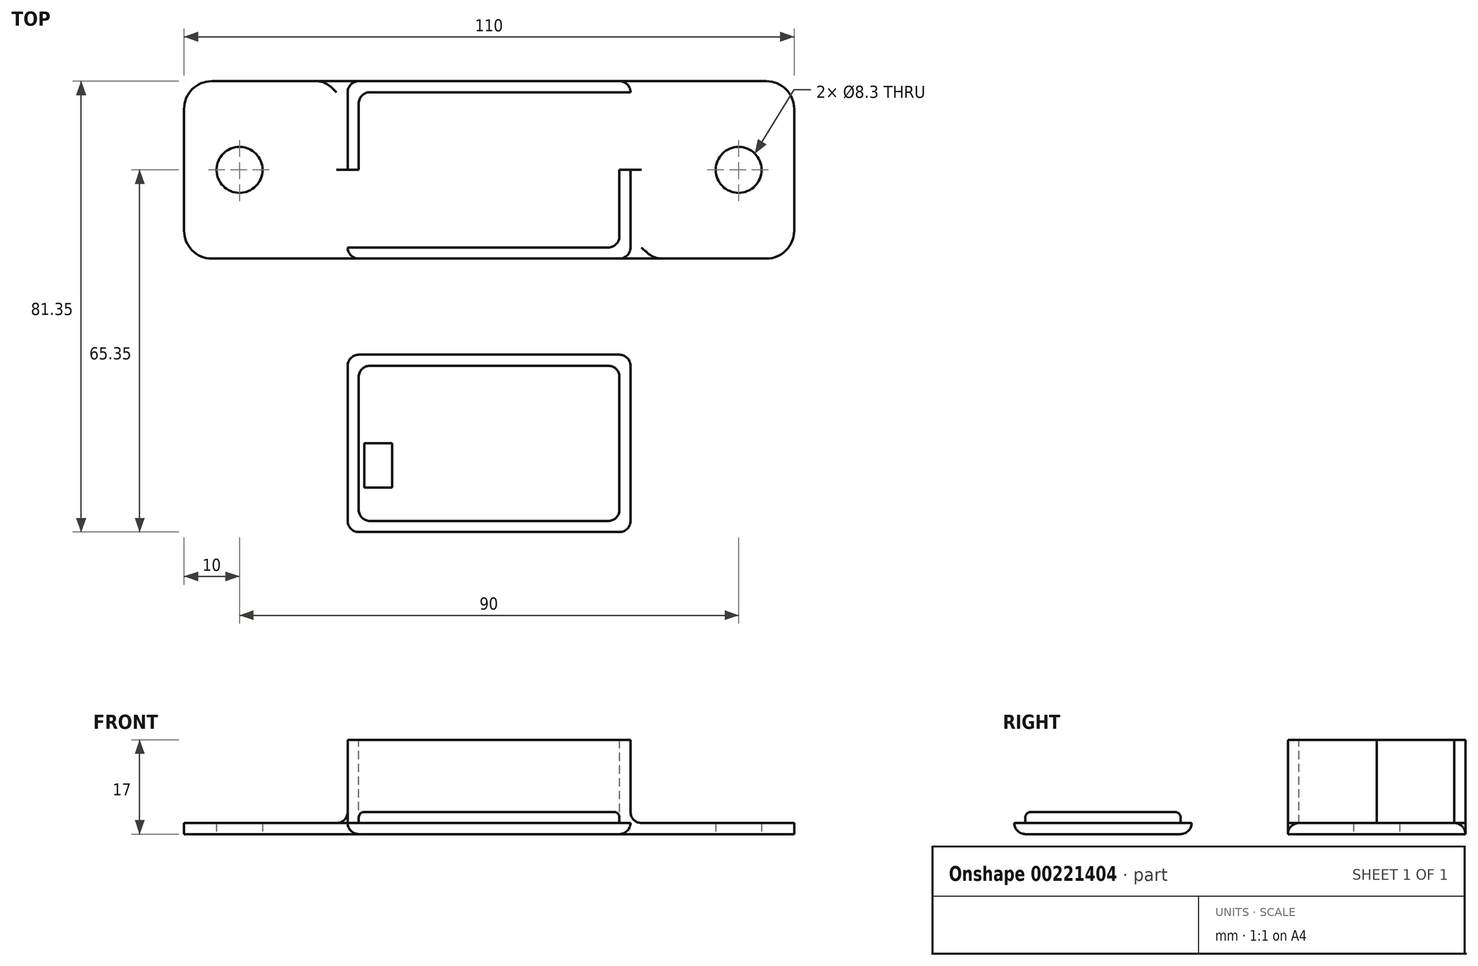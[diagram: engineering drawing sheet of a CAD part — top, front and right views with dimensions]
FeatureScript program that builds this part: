
annotation { "Feature Type Name" : "Feature", "Feature Type Description" : "" }
export const myFeature = defineFeature(function(context is Context, id is Id, definition is map)
    precondition{}
    {
        {
            var Q0;
            Q0=qCreatedBy(makeId("Top.planeOp"),FACE);
            var sketch = newSketch(context, id + "F0", { "sketchPlane" : qUnion([Q0])});
            skLineSegment(sketch, "E0.bottom", {"start": v(55, 16) * mm, "end": v(-55, 16) * mm});
            skLineSegment(sketch, "E0.top", {"start": v(55, -16) * mm, "end": v(-55, -16) * mm});
            skLineSegment(sketch, "E0.left", {"start": v(55, 16) * mm, "end": v(55, -16) * mm});
            skLineSegment(sketch, "E0.right", {"start": v(-55, 16) * mm, "end": v(-55, -16) * mm});
            skPoint(sketch, "E0.middle", {"position": v(0, 0) * mm});
            skLineSegment(sketch, "E1", {"start": v(0, 0) * mm, "end": v(45, 0) * mm});
            skLineSegment(sketch, "E2", {"start": v(0, 0) * mm, "end": v(-45, 0) * mm});
            skCircle(sketch, "E3", {"center": v(-45, 0) * mm, "radius": 4.15 * mm});
            skCircle(sketch, "E4", {"center": v(45, 0) * mm, "radius": 4.15 * mm});
            skSolve(sketch);
        }
        {
            var Q0;
            Q0 = qSketchRegion(id + "F0", true);
            extrude(context, id + "F1", {"entities" : qUnion([Q0]), "depth" : 2 * mm});
        }
        {
            var Q0;
            Q0=makeQuery(id+"F1.opExtrude","CAP_FACE",FACE,{"disambiguationData":[OSD([sQuery(id+"F0.wireOp",EDGE,"E0.bottom"),sQuery(id+"F0.wireOp",EDGE,"E0.top"),sQuery(id+"F0.wireOp",EDGE,"E0.left"),sQuery(id+"F0.wireOp",EDGE,"E0.right")])],"isStart":false});
            var sketch = newSketch(context, id + "F2", { "sketchPlane" : qUnion([Q0])});
            skLineSegment(sketch, "E5", {"start": v(0, -16) * mm, "end": v(0, 16) * mm});
            skLineSegment(sketch, "E6.bottom", {"start": v(23.5, 16) * mm, "end": v(-23.5, 16) * mm});
            skLineSegment(sketch, "E6.top", {"start": v(23.5, -16) * mm, "end": v(-23.5, -16) * mm});
            skLineSegment(sketch, "E6.left", {"start": v(23.5, 16) * mm, "end": v(23.5, -16) * mm});
            skLineSegment(sketch, "E6.right", {"start": v(-23.5, 16) * mm, "end": v(-23.5, -16) * mm});
            skPoint(sketch, "E6.middle", {"position": v(0, 0) * mm});
            skLineSegment(sketch, "E7.bottom", {"start": v(23.5, 14) * mm, "end": v(-23.5, 14) * mm});
            skLineSegment(sketch, "E7.top", {"start": v(23.5, -14) * mm, "end": v(-23.5, -14) * mm});
            skLineSegment(sketch, "E7.left", {"start": v(23.5, 14) * mm, "end": v(23.5, -14) * mm});
            skLineSegment(sketch, "E7.right", {"start": v(-23.5, 14) * mm, "end": v(-23.5, -14) * mm});
            skLineSegment(sketch, "E8.bottom", {"start": v(-25.5, 16) * mm, "end": v(25.5, 16) * mm});
            skLineSegment(sketch, "E8.top", {"start": v(-25.5, -16) * mm, "end": v(25.5, -16) * mm});
            skLineSegment(sketch, "E8.left", {"start": v(-25.5, 16) * mm, "end": v(-25.5, -16) * mm});
            skLineSegment(sketch, "E8.right", {"start": v(25.5, 16) * mm, "end": v(25.5, -16) * mm});
            skSolve(sketch);
        }
        {
            var Q0;
            Q0 = qSketchRegion(id + "F2", true);
            extrude(context, id + "F3", {"entities" : qUnion([Q0]), "operationType" : NewBodyOperationType.ADD, "depth" : 15 * mm});
        }
        {
            var Q0;
            Q0=makeQuery(id+"F3.opExtrude","SWEPT_FACE",FACE,{"disambiguationData":[OSD([sQuery(id+"F2.wireOp",EDGE,"E8.left")])]});
            var sketch = newSketch(context, id + "F4", { "sketchPlane" : qUnion([Q0])});
            skLineSegment(sketch, "E9.bottom", {"start": v(14, 2) * mm, "end": v(0, 2) * mm});
            skLineSegment(sketch, "E9.top", {"start": v(14, 17) * mm, "end": v(0, 17) * mm});
            skLineSegment(sketch, "E9.left", {"start": v(14, 2) * mm, "end": v(14, 17) * mm});
            skLineSegment(sketch, "E9.right", {"start": v(0, 2) * mm, "end": v(0, 17) * mm});
            skSolve(sketch);
        }
        {
            var Q0;
            Q0 = qSketchRegion(id + "F4", true);
            extrude(context, id + "F5", {"entities" : qUnion([Q0]), "operationType" : NewBodyOperationType.REMOVE, "endBound" : BoundingType.UP_TO_NEXT, "oppositeDirection" : true, "depth" : 25 * mm});
        }
        {
            var Q0;
            Q0=makeQuery(id+"F3.opExtrude","SWEPT_FACE",FACE,{"disambiguationData":[OSD([sQuery(id+"F2.wireOp",EDGE,"E8.right")])]});
            var sketch = newSketch(context, id + "F6", { "sketchPlane" : qUnion([Q0])});
            skLineSegment(sketch, "E10.bottom", {"start": v(14, 2) * mm, "end": v(0, 2) * mm});
            skLineSegment(sketch, "E10.top", {"start": v(14, 17) * mm, "end": v(0, 17) * mm});
            skLineSegment(sketch, "E10.left", {"start": v(14, 2) * mm, "end": v(14, 17) * mm});
            skLineSegment(sketch, "E10.right", {"start": v(0, 2) * mm, "end": v(0, 17) * mm});
            skSolve(sketch);
        }
        {
            var Q0;
            Q0 = qSketchRegion(id + "F6", true);
            extrude(context, id + "F7", {"entities" : qUnion([Q0]), "operationType" : NewBodyOperationType.REMOVE, "endBound" : BoundingType.UP_TO_NEXT, "oppositeDirection" : true, "depth" : 25 * mm});
        }
        {
            var Q0;
            Q0=makeQuery(id+"F1.opExtrude","SWEPT_EDGE",EDGE,{"disambiguationData":[OSD([sQuery(id+"F0.wireOp",EDGE,"E0.top"),sQuery(id+"F0.wireOp",EDGE,"E0.right")])]});
            var Q1;
            Q1=makeQuery(id+"F1.opExtrude","SWEPT_EDGE",EDGE,{"disambiguationData":[OSD([sQuery(id+"F0.wireOp",EDGE,"E0.bottom"),sQuery(id+"F0.wireOp",EDGE,"E0.right")])]});
            var Q2;
            Q2=makeQuery(id+"F1.opExtrude","SWEPT_EDGE",EDGE,{"disambiguationData":[OSD([sQuery(id+"F0.wireOp",EDGE,"E0.top"),sQuery(id+"F0.wireOp",EDGE,"E0.left")])]});
            var Q3;
            Q3=makeQuery(id+"F1.opExtrude","SWEPT_EDGE",EDGE,{"disambiguationData":[OSD([sQuery(id+"F0.wireOp",EDGE,"E0.bottom"),sQuery(id+"F0.wireOp",EDGE,"E0.left")])]});
            fillet(context, id + "F8", {"entities" : qUnion([Q0, Q1, Q2, Q3]), "radius" : 5 * mm, "tangentPropagation" : true, "allowEdgeOverflow" : false});
        }
        {
            var Q0;
            Q0=makeQuery(id+"F3.opExtrude","SWEPT_EDGE",EDGE,{"disambiguationData":[OSD([sQuery(id+"F0.wireOp",EDGE,"E0.top"),sQuery(id+"F2.wireOp",EDGE,"E8.top"),sQuery(id+"F2.wireOp",EDGE,"E8.right")])]});
            var Q1;
            Q1=makeQuery(id+"F3.opExtrude","SWEPT_EDGE",EDGE,{"disambiguationData":[OSD([sQuery(id+"F2.wireOp",EDGE,"E6.left"),sQuery(id+"F2.wireOp",EDGE,"E7.top"),sQuery(id+"F2.wireOp",EDGE,"E7.left")])]});
            var Q2;
            Q2=makeQuery(id+"F3.opExtrude","SWEPT_EDGE",EDGE,{"disambiguationData":[OSD([sQuery(id+"F2.wireOp",EDGE,"E6.right"),sQuery(id+"F2.wireOp",EDGE,"E7.bottom"),sQuery(id+"F2.wireOp",EDGE,"E7.right")])]});
            var Q3;
            Q3=makeQuery(id+"F3.opExtrude","SWEPT_EDGE",EDGE,{"disambiguationData":[OSD([sQuery(id+"F0.wireOp",EDGE,"E0.bottom"),sQuery(id+"F2.wireOp",EDGE,"E8.bottom"),sQuery(id+"F2.wireOp",EDGE,"E8.left")])]});
            var Q4;
            {var subQ0=sQuery(id+"F0.wireOp",EDGE,"E0.bottom");var subQ1=sQuery(id+"F2.wireOp",EDGE,"E8.left");Q4=makeQuery(id+"F5.boolean.opBoolean","SPLIT",EDGE,{"disambiguationData":[TD([makeQuery(id+"F1.opExtrude","SWEPT_FACE",FACE,{"disambiguationData":[OSD([subQ0])]})])],"derivedFrom":makeQuery(id+"F3.opExtrude","CAP_EDGE",EDGE,{"disambiguationData":[OSD([subQ1])],"isStart":true})});}
            var Q5;
            {var subQ0=sQuery(id+"F2.wireOp",EDGE,"E8.right");var subQ1=sQuery(id+"F0.wireOp",EDGE,"E0.top");Q5=makeQuery(id+"F7.boolean.opBoolean","SPLIT",EDGE,{"disambiguationData":[TD([makeQuery(id+"F1.opExtrude","SWEPT_FACE",FACE,{"disambiguationData":[OSD([subQ1])]})])],"derivedFrom":makeQuery(id+"F3.opExtrude","CAP_EDGE",EDGE,{"disambiguationData":[OSD([subQ0])],"isStart":true})});}
            var Q6;
            Q6=makeQuery(id+"F3.opExtrude","SWEPT_EDGE",EDGE,{"disambiguationData":[OSD([sQuery(id+"F0.wireOp",EDGE,"E0.bottom"),sQuery(id+"F2.wireOp",EDGE,"E8.bottom"),sQuery(id+"F2.wireOp",EDGE,"E8.right")])]});
            var Q7;
            Q7=makeQuery(id+"F3.opExtrude","SWEPT_EDGE",EDGE,{"disambiguationData":[OSD([sQuery(id+"F0.wireOp",EDGE,"E0.top"),sQuery(id+"F2.wireOp",EDGE,"E8.top"),sQuery(id+"F2.wireOp",EDGE,"E8.left")])]});
            fillet(context, id + "F9", {"entities" : qUnion([Q0, Q1, Q2, Q3, Q4, Q5, Q6, Q7]), "radius" : 2 * mm, "tangentPropagation" : true, "allowEdgeOverflow" : false});
        }
        {
            var Q0;
            Q0=qCreatedBy(makeId("Top.planeOp"),FACE);
            var sketch = newSketch(context, id + "F10", { "sketchPlane" : qUnion([Q0])});
            skLineSegment(sketch, "E11.bottom", {"start": v(23.5, -35.35) * mm, "end": v(-23.5, -35.35) * mm});
            skLineSegment(sketch, "E11.top", {"start": v(23.5, -63.35) * mm, "end": v(-23.5, -63.35) * mm});
            skLineSegment(sketch, "E11.left", {"start": v(23.5, -35.35) * mm, "end": v(23.5, -63.35) * mm});
            skLineSegment(sketch, "E11.right", {"start": v(-23.5, -35.35) * mm, "end": v(-23.5, -63.35) * mm});
            skPoint(sketch, "E11.middle", {"position": v(0, -49.35) * mm});
            skLineSegment(sketch, "E12.bottom", {"start": v(25.5, -33.35) * mm, "end": v(-25.5, -33.35) * mm});
            skLineSegment(sketch, "E12.top", {"start": v(25.5, -65.35) * mm, "end": v(-25.5, -65.35) * mm});
            skLineSegment(sketch, "E12.left", {"start": v(25.5, -33.35) * mm, "end": v(25.5, -65.35) * mm});
            skLineSegment(sketch, "E12.right", {"start": v(-25.5, -33.35) * mm, "end": v(-25.5, -65.35) * mm});
            skSolve(sketch);
        }
        {
            var Q0;
            Q0 = qSketchRegion(id + "F10", true);
            var Q1;
            Q1=makeQuery(id+"F10.imprint","IMPRINT",FACE,{"disambiguationData":[TD([[makeQuery(id+"F10.imprint","IMPRINT",EDGE,{"derivedFrom":sQuery(id+"F10.wireOp",EDGE,"E11.bottom")}),1.0]])]});
            extrude(context, id + "F11", {"entities" : qUnion([Q0, Q1]), "depth" : 2 * mm});
        }
        {
            var Q0;
            Q0=makeQuery(id+"F11.opExtrude","CAP_FACE",FACE,{"disambiguationData":[OSD([sQuery(id+"F10.wireOp",EDGE,"E12.bottom"),sQuery(id+"F10.wireOp",EDGE,"E12.top"),sQuery(id+"F10.wireOp",EDGE,"E12.left"),sQuery(id+"F10.wireOp",EDGE,"E12.right")])],"isStart":false});
            var sketch = newSketch(context, id + "F12", { "sketchPlane" : qUnion([Q0])});
            skLineSegment(sketch, "E13", {"start": v(0, -33.35) * mm, "end": v(0, -65.35) * mm});
            skLineSegment(sketch, "E14.bottom", {"start": v(23.5, -35.35) * mm, "end": v(-23.5, -35.35) * mm});
            skLineSegment(sketch, "E14.top", {"start": v(23.5, -63.35) * mm, "end": v(-23.5, -63.35) * mm});
            skLineSegment(sketch, "E14.left", {"start": v(23.5, -35.35) * mm, "end": v(23.5, -63.35) * mm});
            skLineSegment(sketch, "E14.right", {"start": v(-23.5, -35.35) * mm, "end": v(-23.5, -63.35) * mm});
            skPoint(sketch, "E14.middle", {"position": v(0, -49.35) * mm});
            skSolve(sketch);
        }
        {
            var Q0;
            Q0 = qSketchRegion(id + "F12", true);
            extrude(context, id + "F13", {"entities" : qUnion([Q0]), "operationType" : NewBodyOperationType.ADD, "depth" : 2 * mm});
        }
        {
            var Q0;
            Q0=makeQuery(id+"F13.opExtrude","SWEPT_EDGE",EDGE,{"disambiguationData":[OSD([sQuery(id+"F12.wireOp",EDGE,"E14.top"),sQuery(id+"F12.wireOp",EDGE,"E14.right")])]});
            var Q1;
            Q1=makeQuery(id+"F11.opExtrude","SWEPT_EDGE",EDGE,{"disambiguationData":[OSD([sQuery(id+"F10.wireOp",EDGE,"E12.top"),sQuery(id+"F10.wireOp",EDGE,"E12.right")])]});
            var Q2;
            Q2=makeQuery(id+"F13.opExtrude","SWEPT_EDGE",EDGE,{"disambiguationData":[OSD([sQuery(id+"F12.wireOp",EDGE,"E14.top"),sQuery(id+"F12.wireOp",EDGE,"E14.left")])]});
            var Q3;
            Q3=makeQuery(id+"F13.opExtrude","SWEPT_EDGE",EDGE,{"disambiguationData":[OSD([sQuery(id+"F12.wireOp",EDGE,"E14.bottom"),sQuery(id+"F12.wireOp",EDGE,"E14.left")])]});
            var Q4;
            Q4=makeQuery(id+"F13.opExtrude","SWEPT_EDGE",EDGE,{"disambiguationData":[OSD([sQuery(id+"F12.wireOp",EDGE,"E14.bottom"),sQuery(id+"F12.wireOp",EDGE,"E14.right")])]});
            var Q5;
            Q5=makeQuery(id+"F11.opExtrude","SWEPT_EDGE",EDGE,{"disambiguationData":[OSD([sQuery(id+"F10.wireOp",EDGE,"E12.bottom"),sQuery(id+"F10.wireOp",EDGE,"E12.right")])]});
            var Q6;
            Q6=makeQuery(id+"F11.opExtrude","SWEPT_EDGE",EDGE,{"disambiguationData":[OSD([sQuery(id+"F10.wireOp",EDGE,"E12.bottom"),sQuery(id+"F10.wireOp",EDGE,"E12.left")])]});
            var Q7;
            Q7=makeQuery(id+"F11.opExtrude","SWEPT_EDGE",EDGE,{"disambiguationData":[OSD([sQuery(id+"F10.wireOp",EDGE,"E12.top"),sQuery(id+"F10.wireOp",EDGE,"E12.left")])]});
            var Q8;
            Q8=makeQuery(id+"F11.opExtrude","CAP_EDGE",EDGE,{"disambiguationData":[OSD([sQuery(id+"F10.wireOp",EDGE,"E12.top")])],"isStart":true});
            var Q9;
            Q9=makeQuery(id+"F11.opExtrude","CAP_EDGE",EDGE,{"disambiguationData":[OSD([sQuery(id+"F10.wireOp",EDGE,"E12.left")])],"isStart":true});
            var Q10;
            Q10=makeQuery(id+"F11.opExtrude","CAP_EDGE",EDGE,{"disambiguationData":[OSD([sQuery(id+"F10.wireOp",EDGE,"E12.bottom")])],"isStart":true});
            var Q11;
            Q11=makeQuery(id+"F11.opExtrude","CAP_EDGE",EDGE,{"disambiguationData":[OSD([sQuery(id+"F10.wireOp",EDGE,"E12.right")])],"isStart":true});
            fillet(context, id + "F14", {"entities" : qUnion([Q0, Q1, Q2, Q3, Q4, Q5, Q6, Q7, Q8, Q9, Q10, Q11]), "radius" : 2 * mm, "tangentPropagation" : true, "allowEdgeOverflow" : false});
        }
        {
            var Q0;
            Q0=makeQuery(id+"F13.opExtrude","CAP_FACE",FACE,{"disambiguationData":[OSD([sQuery(id+"F12.wireOp",EDGE,"E14.bottom"),sQuery(id+"F12.wireOp",EDGE,"E14.top"),sQuery(id+"F12.wireOp",EDGE,"E14.left"),sQuery(id+"F12.wireOp",EDGE,"E14.right")])],"isStart":false});
            fillet(context, id + "F15", {"entities" : qUnion([Q0]), "radius" : 1 * mm, "tangentPropagation" : true, "allowEdgeOverflow" : false});
        }
        {
            var Q0;
            Q0=makeQuery(id+"F13.opExtrude","CAP_FACE",FACE,{"disambiguationData":[OSD([sQuery(id+"F12.wireOp",EDGE,"E14.bottom"),sQuery(id+"F12.wireOp",EDGE,"E14.top"),sQuery(id+"F12.wireOp",EDGE,"E14.left"),sQuery(id+"F12.wireOp",EDGE,"E14.right")])],"isStart":false});
            var sketch = newSketch(context, id + "F16", { "sketchPlane" : qUnion([Q0])});
            skLineSegment(sketch, "E15.bottom", {"start": v(-22.5, -49.35) * mm, "end": v(-17.5, -49.35) * mm});
            skLineSegment(sketch, "E15.top", {"start": v(-22.5, -57.35) * mm, "end": v(-17.5, -57.35) * mm});
            skLineSegment(sketch, "E15.left", {"start": v(-22.5, -49.35) * mm, "end": v(-22.5, -57.35) * mm});
            skLineSegment(sketch, "E15.right", {"start": v(-17.5, -49.35) * mm, "end": v(-17.5, -57.35) * mm});
            skSolve(sketch);
        }
        {
            var Q0;
            Q0 = qSketchRegion(id + "F16", true);
            extrude(context, id + "F17", {"entities" : qUnion([Q0]), "operationType" : NewBodyOperationType.REMOVE, "oppositeDirection" : true, "depth" : 25 * mm});
        }
    });
